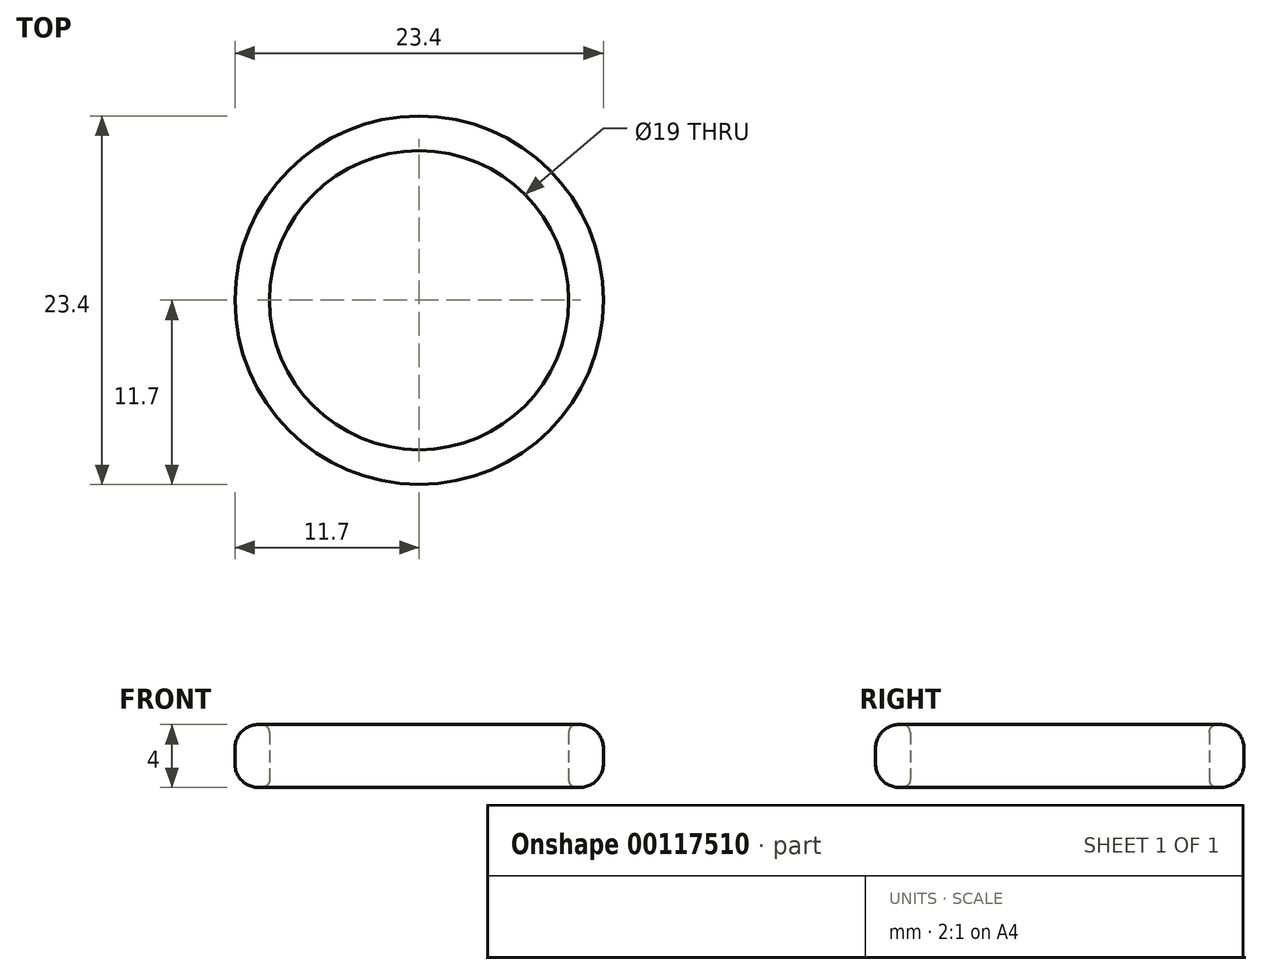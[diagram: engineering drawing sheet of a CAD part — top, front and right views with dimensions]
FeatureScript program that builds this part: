
annotation { "Feature Type Name" : "Feature", "Feature Type Description" : "" }
export const myFeature = defineFeature(function(context is Context, id is Id, definition is map)
    precondition{}
    {
        {
            var Q0;
            Q0=qCreatedBy(makeId("Top.planeOp"),FACE);
            var sketch = newSketch(context, id + "F0", { "sketchPlane" : qUnion([Q0])});
            skCircle(sketch, "E0", {"center": v(0, 0) * mm, "radius": 9.5 * mm});
            skCircle(sketch, "E1", {"center": v(0, 0) * mm, "radius": 11.7 * mm});
            skSolve(sketch);
        }
        {
            var Q0;
            Q0=makeQuery(id+"F0.imprint","IMPRINT",FACE,{"disambiguationData":[TD([[makeQuery(id+"F0.imprint","IMPRINT",EDGE,{"derivedFrom":sQuery(id+"F0.wireOp",EDGE,"E0")}),-1.0]])]});
            extrude(context, id + "F1", {"entities" : qUnion([Q0]), "depth" : 4 * mm});
        }
        {
            var Q0;
            Q0=makeQuery(id+"F1.opExtrude","CAP_EDGE",EDGE,{"disambiguationData":[OSD([sQuery(id+"F0.wireOp",EDGE,"E0")])],"isStart":false});
            var Q1;
            Q1=makeQuery(id+"F1.opExtrude","CAP_EDGE",EDGE,{"disambiguationData":[OSD([sQuery(id+"F0.wireOp",EDGE,"E0")])],"isStart":true});
            fillet(context, id + "F2", {"entities" : qUnion([Q0, Q1]), "radius" : 0.5 * mm, "tangentPropagation" : true, "allowEdgeOverflow" : false});
        }
        {
            var Q0;
            Q0=makeQuery(id+"F1.opExtrude","CAP_EDGE",EDGE,{"disambiguationData":[OSD([sQuery(id+"F0.wireOp",EDGE,"E1")])],"isStart":false});
            var Q1;
            Q1=makeQuery(id+"F1.opExtrude","CAP_EDGE",EDGE,{"disambiguationData":[OSD([sQuery(id+"F0.wireOp",EDGE,"E1")])],"isStart":true});
            fillet(context, id + "F3", {"entities" : qUnion([Q0, Q1]), "radius" : 1.5 * mm, "tangentPropagation" : true, "allowEdgeOverflow" : false});
        }
    });
